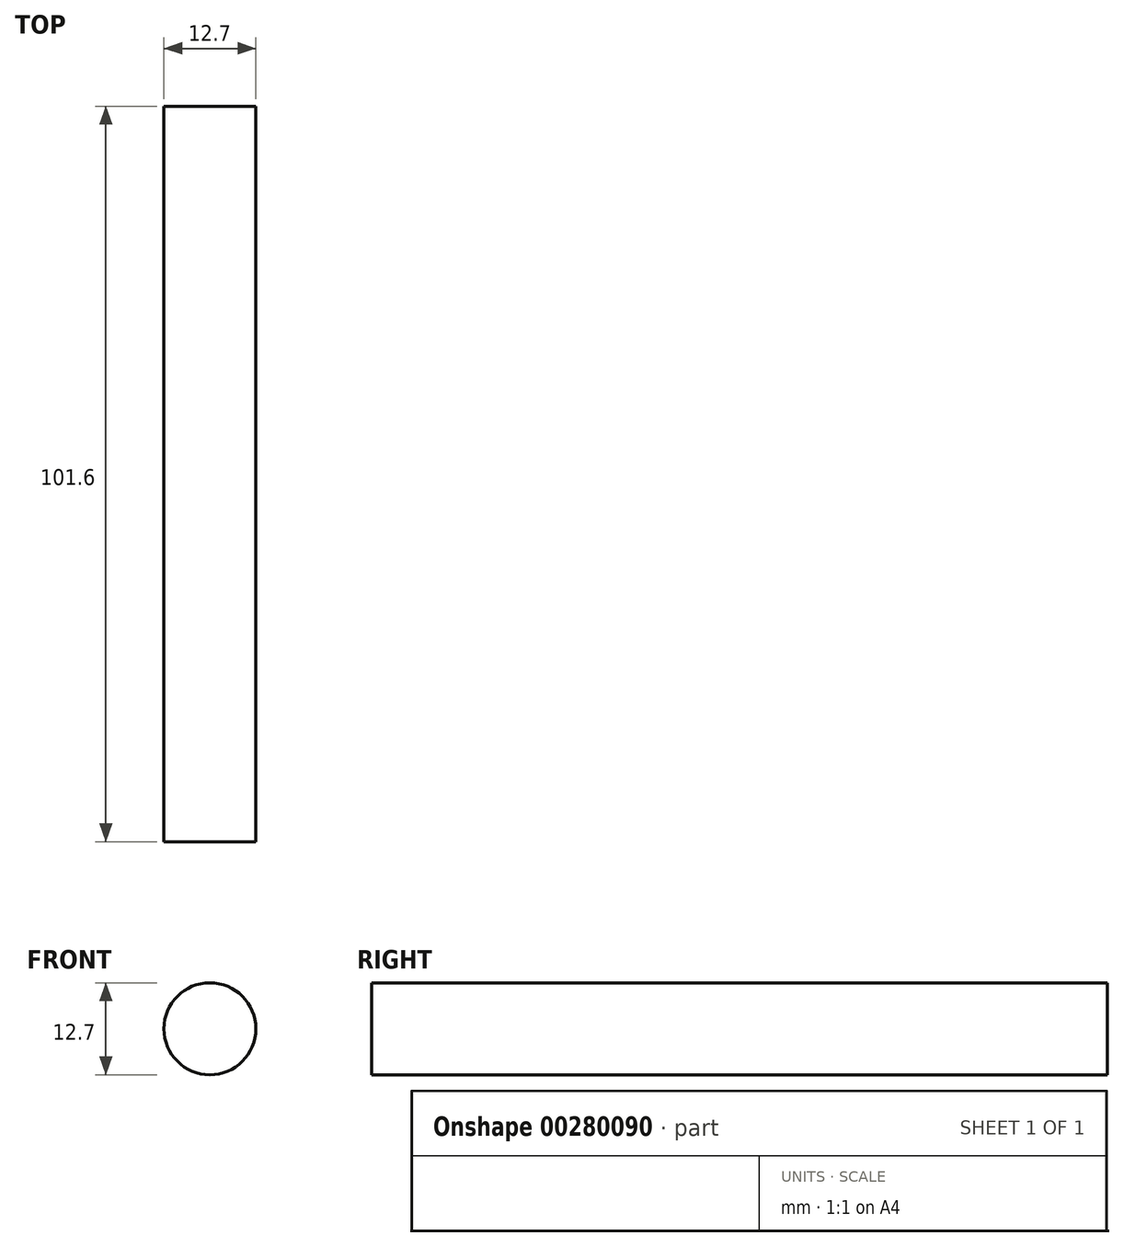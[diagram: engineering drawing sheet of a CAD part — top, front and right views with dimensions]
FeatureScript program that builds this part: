
annotation { "Feature Type Name" : "Feature", "Feature Type Description" : "" }
export const myFeature = defineFeature(function(context is Context, id is Id, definition is map)
    precondition{}
    {
        {
            var Q0;
            Q0=qCreatedBy(makeId("Front.planeOp"),FACE);
            var sketch = newSketch(context, id + "F0", { "sketchPlane" : qUnion([Q0])});
            skCircle(sketch, "E0", {"center": v(0, 0) * mm, "radius": 6.35 * mm});
            skSolve(sketch);
        }
        {
            var Q0;
            Q0 = qSketchRegion(id + "F0", true);
            extrude(context, id + "F1", {"entities" : qUnion([Q0]), "depth" : 101.6 * mm});
        }
    });
